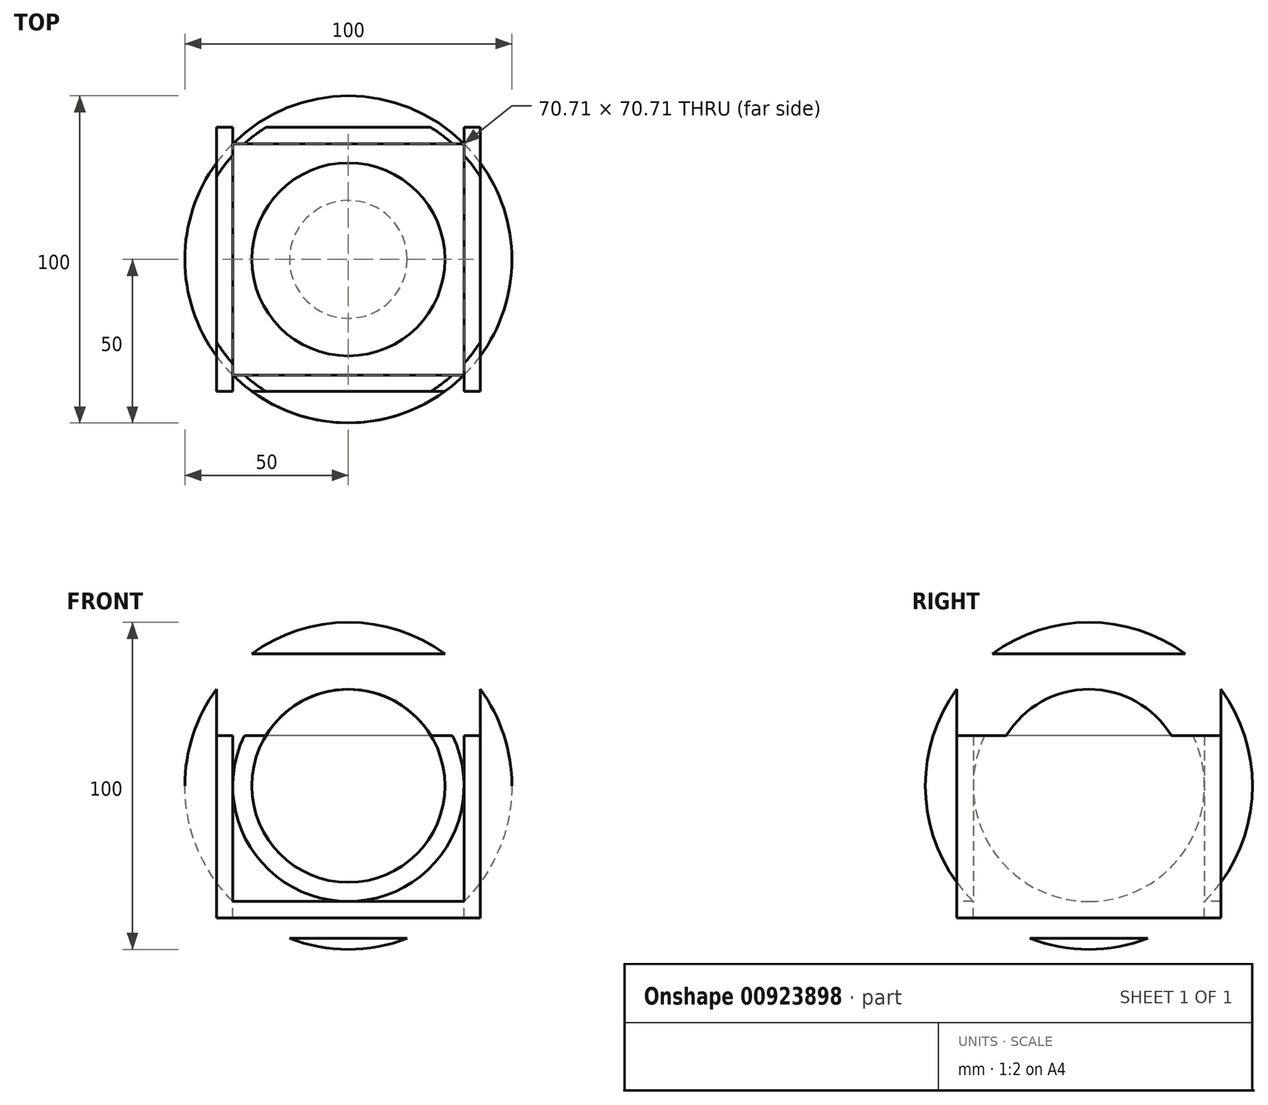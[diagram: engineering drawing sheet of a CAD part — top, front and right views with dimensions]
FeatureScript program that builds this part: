
annotation { "Feature Type Name" : "Feature", "Feature Type Description" : "" }
export const myFeature = defineFeature(function(context is Context, id is Id, definition is map)
    precondition{}
    {
        {
            var Q0;
            Q0=qCreatedBy(makeId("Front.planeOp"),FACE);
            var sketch = newSketch(context, id + "F0", { "sketchPlane" : qUnion([Q0])});
            skCircle(sketch, "E0", {"center": v(0, 0) * mm, "radius": 50 * mm});
            skLineSegment(sketch, "E1.bottom", {"start": v(40.36, -40.36) * mm, "end": v(-40.36, -40.36) * mm});
            skLineSegment(sketch, "E1.top", {"start": v(40.36, 40.36) * mm, "end": v(-40.36, 40.36) * mm});
            skLineSegment(sketch, "E1.left", {"start": v(40.36, -40.36) * mm, "end": v(40.36, 40.36) * mm});
            skLineSegment(sketch, "E1.right", {"start": v(-40.36, -40.36) * mm, "end": v(-40.36, 40.36) * mm});
            skLineSegment(sketch, "E2.0", {"start": v(35.36, 35.36) * mm, "end": v(-35.36, 35.36) * mm});
            skLineSegment(sketch, "E2.1", {"start": v(35.36, -35.36) * mm, "end": v(35.36, 35.36) * mm});
            skLineSegment(sketch, "E2.2", {"start": v(35.36, -35.36) * mm, "end": v(-35.36, -35.36) * mm});
            skLineSegment(sketch, "E2.3", {"start": v(-35.36, -35.36) * mm, "end": v(-35.36, 35.36) * mm});
            skLineSegment(sketch, "E3", {"start": v(0, 0) * mm, "end": v(0, 62.81) * mm, "construction": true});
            skLineSegment(sketch, "E4", {"start": v(0, 0) * mm, "end": v(91.75, 0) * mm, "construction": true});
            skLineSegment(sketch, "E5.bottom", {"start": v(35.36, 35.36) * mm, "end": v(40.36, 35.36) * mm});
            skLineSegment(sketch, "E5.top", {"start": v(35.36, 40.36) * mm, "end": v(40.36, 40.36) * mm});
            skLineSegment(sketch, "E5.left", {"start": v(35.36, 35.36) * mm, "end": v(35.36, 40.36) * mm});
            skLineSegment(sketch, "E5.right", {"start": v(40.36, 35.36) * mm, "end": v(40.36, 40.36) * mm});
            skLineSegment(sketch, "E6.bottom", {"start": v(-40.36, 40.36) * mm, "end": v(-35.36, 40.36) * mm});
            skLineSegment(sketch, "E6.top", {"start": v(-40.36, 35.36) * mm, "end": v(-35.36, 35.36) * mm});
            skLineSegment(sketch, "E6.left", {"start": v(-40.36, 40.36) * mm, "end": v(-40.36, 35.36) * mm});
            skLineSegment(sketch, "E6.right", {"start": v(-35.36, 40.36) * mm, "end": v(-35.36, 35.36) * mm});
            skLineSegment(sketch, "E7.bottom", {"start": v(-40.36, -40.36) * mm, "end": v(-35.36, -40.36) * mm});
            skLineSegment(sketch, "E7.top", {"start": v(-40.36, -35.36) * mm, "end": v(-35.36, -35.36) * mm});
            skLineSegment(sketch, "E7.left", {"start": v(-40.36, -40.36) * mm, "end": v(-40.36, -35.36) * mm});
            skLineSegment(sketch, "E7.right", {"start": v(-35.36, -40.36) * mm, "end": v(-35.36, -35.36) * mm});
            skLineSegment(sketch, "E8.bottom", {"start": v(35.36, -35.36) * mm, "end": v(40.36, -35.36) * mm});
            skLineSegment(sketch, "E8.top", {"start": v(35.36, -40.36) * mm, "end": v(40.36, -40.36) * mm});
            skLineSegment(sketch, "E8.left", {"start": v(35.36, -35.36) * mm, "end": v(35.36, -40.36) * mm});
            skLineSegment(sketch, "E8.right", {"start": v(40.36, -35.36) * mm, "end": v(40.36, -40.36) * mm});
            skSolve(sketch);
        }
        {
            var Q0;
            Q0=qCreatedBy(makeId("Right.planeOp"),FACE);
            var sketch = newSketch(context, id + "F1", { "sketchPlane" : qUnion([Q0])});
            skCircle(sketch, "E9", {"center": v(0, 0) * mm, "radius": 50 * mm});
            skLineSegment(sketch, "E10.bottom", {"start": v(40.36, 40.36) * mm, "end": v(-40.36, 40.36) * mm});
            skLineSegment(sketch, "E10.top", {"start": v(40.36, -40.36) * mm, "end": v(-40.36, -40.36) * mm});
            skLineSegment(sketch, "E10.left", {"start": v(40.36, 40.36) * mm, "end": v(40.36, -40.36) * mm});
            skLineSegment(sketch, "E10.right", {"start": v(-40.36, 40.36) * mm, "end": v(-40.36, -40.36) * mm});
            skLineSegment(sketch, "E11.0", {"start": v(35.36, 35.36) * mm, "end": v(-35.36, 35.36) * mm});
            skLineSegment(sketch, "E11.1", {"start": v(35.36, 35.36) * mm, "end": v(35.36, -35.36) * mm});
            skLineSegment(sketch, "E11.2", {"start": v(35.36, -35.36) * mm, "end": v(-35.36, -35.36) * mm});
            skLineSegment(sketch, "E11.3", {"start": v(-35.36, 35.36) * mm, "end": v(-35.36, -35.36) * mm});
            skLineSegment(sketch, "E12.bottom", {"start": v(-40.36, 40.36) * mm, "end": v(-35.36, 40.36) * mm});
            skLineSegment(sketch, "E12.top", {"start": v(-40.36, 35.36) * mm, "end": v(-35.36, 35.36) * mm});
            skLineSegment(sketch, "E12.left", {"start": v(-40.36, 40.36) * mm, "end": v(-40.36, 35.36) * mm});
            skLineSegment(sketch, "E12.right", {"start": v(-35.36, 40.36) * mm, "end": v(-35.36, 35.36) * mm});
            skLineSegment(sketch, "E13.bottom", {"start": v(40.36, 40.36) * mm, "end": v(35.36, 40.36) * mm});
            skLineSegment(sketch, "E13.top", {"start": v(40.36, 35.36) * mm, "end": v(35.36, 35.36) * mm});
            skLineSegment(sketch, "E13.left", {"start": v(40.36, 40.36) * mm, "end": v(40.36, 35.36) * mm});
            skLineSegment(sketch, "E13.right", {"start": v(35.36, 40.36) * mm, "end": v(35.36, 35.36) * mm});
            skLineSegment(sketch, "E14.bottom", {"start": v(40.36, -40.36) * mm, "end": v(35.36, -40.36) * mm});
            skLineSegment(sketch, "E14.top", {"start": v(40.36, -35.36) * mm, "end": v(35.36, -35.36) * mm});
            skLineSegment(sketch, "E14.left", {"start": v(40.36, -40.36) * mm, "end": v(40.36, -35.36) * mm});
            skLineSegment(sketch, "E14.right", {"start": v(35.36, -40.36) * mm, "end": v(35.36, -35.36) * mm});
            skLineSegment(sketch, "E15.bottom", {"start": v(-40.36, -40.36) * mm, "end": v(-35.36, -40.36) * mm});
            skLineSegment(sketch, "E15.top", {"start": v(-40.36, -35.36) * mm, "end": v(-35.36, -35.36) * mm});
            skLineSegment(sketch, "E15.left", {"start": v(-40.36, -40.36) * mm, "end": v(-40.36, -35.36) * mm});
            skLineSegment(sketch, "E15.right", {"start": v(-35.36, -40.36) * mm, "end": v(-35.36, -35.36) * mm});
            skSolve(sketch);
        }
        {
            var Q0;
            Q0=qCreatedBy(makeId("Front.planeOp"),FACE);
            var sketch = newSketch(context, id + "F2", { "sketchPlane" : qUnion([Q0])});
            skArc(sketch, "E16.0", {"start": v(50, 0) * mm, "mid": v(0, 50) * mm, "end": v(-50, 0) * mm});
            skLineSegment(sketch, "E17", {"start": v(-50, 0) * mm, "end": v(50, 0) * mm});
            skSolve(sketch);
        }
        {
            var Q0;
            Q0 = qSketchRegion(id + "F2", true);
            var Q1;
            Q1=sQuery(id+"F0.wireOp",EDGE,"E4");
            revolve(context, id + "F3", {"surfaceOperationType" : NewSurfaceOperationType.NEW, "entities" : qUnion([Q0]), "axis" : qUnion([Q1]), "revolveType" : RevolveType.FULL});
        }
        {
            var Q0;
            Q0=qCreatedBy(makeId("Front.planeOp"),FACE);
            var sketch = newSketch(context, id + "F4", { "sketchPlane" : qUnion([Q0])});
            skLineSegment(sketch, "E18.0", {"start": v(40.36, -40.36) * mm, "end": v(40.36, 40.36) * mm});
            skLineSegment(sketch, "E18.1", {"start": v(40.36, -40.36) * mm, "end": v(-40.36, -40.36) * mm});
            skLineSegment(sketch, "E18.2", {"start": v(-40.36, -40.36) * mm, "end": v(-40.36, 40.36) * mm});
            skLineSegment(sketch, "E18.3", {"start": v(40.36, 40.36) * mm, "end": v(-40.36, 40.36) * mm});
            skSolve(sketch);
        }
        {
            var Q0;
            Q0 = qSketchRegion(id + "F4", true);
            var Q1;
            Q1=sQuery(id+"F1.wireOp",VERTEX,"E10.top.start");
            var Q2;
            Q2=sQuery(id+"F1.wireOp",VERTEX,"E10.top.end");
            extrude(context, id + "F5", {"entities" : qUnion([Q0]), "endBound" : BoundingType.UP_TO_VERTEX, "oppositeDirection" : true, "depth" : 25 * mm, "endBoundEntityVertex" : qUnion([Q1]), "offsetDistance" : 25 * mm, "hasSecondDirection" : true, "secondDirectionBound" : SecondDirectionBoundingType.UP_TO_VERTEX, "secondDirectionOppositeDirection" : false, "secondDirectionDepth" : 25 * mm, "secondDirectionBoundEntityVertex" : qUnion([Q2])});
        }
        {
            var Q0;
            {var subQ3=sQuery(id+"F0.wireOp",EDGE,"E2.0");Q0=makeQuery(id+"F0.imprint","IMPRINT",FACE,{"disambiguationData":[TD([[makeQuery(id+"F0.imprint","IMPRINT",EDGE,{"derivedFrom":subQ3}),-1.0]])]});}
            var Q1;
            {var subQ0=sQuery(id+"F0.wireOp",EDGE,"E6.right");Q1=makeQuery(id+"F0.imprint","IMPRINT",FACE,{"disambiguationData":[TD([[makeQuery(id+"F0.imprint","IMPRINT",EDGE,{"derivedFrom":subQ0}),1.0]])]});}
            var Q2;
            {var subQ4=sQuery(id+"F0.wireOp",EDGE,"E6.top");Q2=makeQuery(id+"F0.imprint","IMPRINT",FACE,{"disambiguationData":[TD([[makeQuery(id+"F0.imprint","IMPRINT",EDGE,{"derivedFrom":subQ4}),1.0]])]});}
            var Q3;
            {var subQ0=sQuery(id+"F0.wireOp",EDGE,"E6.top");Q3=makeQuery(id+"F0.imprint","IMPRINT",FACE,{"disambiguationData":[TD([[makeQuery(id+"F0.imprint","IMPRINT",EDGE,{"derivedFrom":subQ0}),-1.0]])]});}
            var Q4;
            {var subQ0=sQuery(id+"F0.wireOp",EDGE,"E2.3");Q4=makeQuery(id+"F0.imprint","IMPRINT",FACE,{"disambiguationData":[TD([[makeQuery(id+"F0.imprint","IMPRINT",EDGE,{"derivedFrom":subQ0}),1.0]])]});}
            var Q5;
            {var subQ3=sQuery(id+"F0.wireOp",EDGE,"E7.top");Q5=makeQuery(id+"F0.imprint","IMPRINT",FACE,{"disambiguationData":[TD([[makeQuery(id+"F0.imprint","IMPRINT",EDGE,{"derivedFrom":subQ3}),1.0]])]});}
            var Q6;
            {var subQ4=sQuery(id+"F0.wireOp",EDGE,"E7.top");Q6=makeQuery(id+"F0.imprint","IMPRINT",FACE,{"disambiguationData":[TD([[makeQuery(id+"F0.imprint","IMPRINT",EDGE,{"derivedFrom":subQ4}),-1.0]])]});}
            var Q7;
            {var subQ0=sQuery(id+"F0.wireOp",EDGE,"E7.right");Q7=makeQuery(id+"F0.imprint","IMPRINT",FACE,{"disambiguationData":[TD([[makeQuery(id+"F0.imprint","IMPRINT",EDGE,{"derivedFrom":subQ0}),-1.0]])]});}
            var Q8;
            {var subQ3=sQuery(id+"F0.wireOp",EDGE,"E2.2");Q8=makeQuery(id+"F0.imprint","IMPRINT",FACE,{"disambiguationData":[TD([[makeQuery(id+"F0.imprint","IMPRINT",EDGE,{"derivedFrom":subQ3}),1.0]])]});}
            var Q9;
            {var subQ3=sQuery(id+"F0.wireOp",EDGE,"E8.left");Q9=makeQuery(id+"F0.imprint","IMPRINT",FACE,{"disambiguationData":[TD([[makeQuery(id+"F0.imprint","IMPRINT",EDGE,{"derivedFrom":subQ3}),-1.0]])]});}
            var Q10;
            {var subQ4=sQuery(id+"F0.wireOp",EDGE,"E8.bottom");Q10=makeQuery(id+"F0.imprint","IMPRINT",FACE,{"disambiguationData":[TD([[makeQuery(id+"F0.imprint","IMPRINT",EDGE,{"derivedFrom":subQ4}),-1.0]])]});}
            var Q11;
            {var subQ3=sQuery(id+"F0.wireOp",EDGE,"E8.bottom");Q11=makeQuery(id+"F0.imprint","IMPRINT",FACE,{"disambiguationData":[TD([[makeQuery(id+"F0.imprint","IMPRINT",EDGE,{"derivedFrom":subQ3}),1.0]])]});}
            var Q12;
            {var subQ3=sQuery(id+"F0.wireOp",EDGE,"E2.1");Q12=makeQuery(id+"F0.imprint","IMPRINT",FACE,{"disambiguationData":[TD([[makeQuery(id+"F0.imprint","IMPRINT",EDGE,{"derivedFrom":subQ3}),-1.0]])]});}
            var Q13;
            {var subQ3=sQuery(id+"F0.wireOp",EDGE,"E5.left");Q13=makeQuery(id+"F0.imprint","IMPRINT",FACE,{"disambiguationData":[TD([[makeQuery(id+"F0.imprint","IMPRINT",EDGE,{"derivedFrom":subQ3}),1.0]])]});}
            var Q14;
            {var subQ4=sQuery(id+"F0.wireOp",EDGE,"E5.bottom");Q14=makeQuery(id+"F0.imprint","IMPRINT",FACE,{"disambiguationData":[TD([[makeQuery(id+"F0.imprint","IMPRINT",EDGE,{"derivedFrom":subQ4}),1.0]])]});}
            var Q15;
            {var subQ0=sQuery(id+"F0.wireOp",EDGE,"E5.bottom");Q15=makeQuery(id+"F0.imprint","IMPRINT",FACE,{"disambiguationData":[TD([[makeQuery(id+"F0.imprint","IMPRINT",EDGE,{"derivedFrom":subQ0}),-1.0]])]});}
            var Q16;
            Q16=sQuery(id+"F1.wireOp",VERTEX,"E10.bottom.end");
            var Q17;
            Q17=sQuery(id+"F1.wireOp",VERTEX,"E10.top.start");
            extrude(context, id + "F6", {"entities" : qUnion([Q0, Q1, Q2, Q3, Q4, Q5, Q6, Q7, Q8, Q9, Q10, Q11, Q12, Q13, Q14, Q15]), "endBound" : BoundingType.UP_TO_VERTEX, "depth" : 25 * mm, "endBoundEntityVertex" : qUnion([Q16]), "offsetDistance" : 25 * mm, "hasSecondDirection" : true, "secondDirectionBound" : SecondDirectionBoundingType.UP_TO_VERTEX, "secondDirectionOppositeDirection" : true, "secondDirectionDepth" : 25 * mm, "secondDirectionBoundEntityVertex" : qUnion([Q17])});
        }
        {
            var Q0;
            Q0=sQuery(id+"F1.wireOp",EDGE,"E10.bottom");
            var Q1;
            Q1=sQuery(id+"F1.wireOp",EDGE,"E10.right");
            var Q2;
            Q2=sQuery(id+"F1.wireOp",EDGE,"E11.3");
            var Q3;
            Q3=sQuery(id+"F1.wireOp",EDGE,"E11.0");
            var Q4;
            Q4=sQuery(id+"F1.wireOp",EDGE,"E11.1");
            var Q5;
            Q5=sQuery(id+"F1.wireOp",EDGE,"E10.left");
            var Q6;
            Q6=sQuery(id+"F1.wireOp",EDGE,"E10.top");
            var Q7;
            Q7=sQuery(id+"F1.wireOp",EDGE,"E11.2");
            var Q8;
            Q8=makeQuery(id+"F6.opExtrude","CAP_VERTEX",VERTEX,{"disambiguationData":[OSD([sQuery(id+"F0.wireOp",EDGE,"E1.top"),sQuery(id+"F0.wireOp",EDGE,"E1.left")])],"isStart":true});
            var Q9;
            Q9=makeQuery(id+"F6.opExtrude","CAP_VERTEX",VERTEX,{"disambiguationData":[OSD([sQuery(id+"F0.wireOp",EDGE,"E1.top"),sQuery(id+"F0.wireOp",EDGE,"E1.right")])],"isStart":true});
            extrude(context, id + "F7", {"bodyType" : ToolBodyType.SURFACE, "surfaceEntities" : qUnion([Q0, Q1, Q2, Q3, Q4, Q5, Q6, Q7]), "endBound" : BoundingType.UP_TO_VERTEX, "depth" : 25 * mm, "endBoundEntityVertex" : qUnion([Q8]), "offsetDistance" : 25 * mm, "hasSecondDirection" : true, "secondDirectionBound" : SecondDirectionBoundingType.UP_TO_VERTEX, "secondDirectionOppositeDirection" : true, "secondDirectionDepth" : 25 * mm, "secondDirectionBoundEntityVertex" : qUnion([Q9])});
        }
        {
            var Q0;
            Q0=makeQuery(id+"F5.opExtrude","CAP_FACE",FACE,{"disambiguationData":[OSD([sQuery(id+"F4.wireOp",EDGE,"E18.0"),sQuery(id+"F4.wireOp",EDGE,"E18.1"),sQuery(id+"F4.wireOp",EDGE,"E18.2"),sQuery(id+"F4.wireOp",EDGE,"E18.3")])],"isStart":true});
            var sketch = newSketch(context, id + "F8", { "sketchPlane" : qUnion([Q0])});
            skLineSegment(sketch, "E19.0", {"start": v(35.36, 35.36) * mm, "end": v(-35.36, 35.36) * mm});
            skLineSegment(sketch, "E19.1", {"start": v(-35.36, -35.36) * mm, "end": v(-35.36, 35.36) * mm});
            skLineSegment(sketch, "E19.2", {"start": v(35.36, -35.36) * mm, "end": v(35.36, 35.36) * mm});
            skLineSegment(sketch, "E19.3", {"start": v(35.36, -35.36) * mm, "end": v(-35.36, -35.36) * mm});
            skSolve(sketch);
        }
        {
            var Q0;
            Q0 = qSketchRegion(id + "F8", true);
            extrude(context, id + "F9", {"entities" : qUnion([Q0]), "operationType" : NewBodyOperationType.REMOVE, "endBound" : BoundingType.THROUGH_ALL, "oppositeDirection" : true, "depth" : 25 * mm, "offsetDistance" : 25 * mm});
        }
        {
            var Q0;
            Q0 = qSketchRegion(id + "F2", true);
            var Q1;
            Q1=sQuery(id+"F0.wireOp",EDGE,"E4");
            revolve(context, id + "F10", {"surfaceOperationType" : NewSurfaceOperationType.NEW, "entities" : qUnion([Q0]), "axis" : qUnion([Q1]), "revolveType" : RevolveType.FULL});
        }
        {
            var Q0;
            Q0=makeQuery(id+"F5.opExtrude","SWEPT_FACE",FACE,{"disambiguationData":[OSD([sQuery(id+"F4.wireOp",EDGE,"E18.3")])]});
            var sketch = newSketch(context, id + "F11", { "sketchPlane" : qUnion([Q0])});
            skLineSegment(sketch, "E20.1", {"start": v(-40.36, 40.36) * mm, "end": v(-40.36, -40.36) * mm});
            skLineSegment(sketch, "E20.2", {"start": v(40.36, 40.36) * mm, "end": v(-40.36, 40.36) * mm});
            skLineSegment(sketch, "E20.3", {"start": v(40.36, 40.36) * mm, "end": v(40.36, -40.36) * mm});
            skLineSegment(sketch, "E20.4", {"start": v(40.36, -40.36) * mm, "end": v(-40.36, -40.36) * mm});
            skLineSegment(sketch, "E21.0", {"start": v(35.36, 35.36) * mm, "end": v(-35.36, 35.36) * mm});
            skLineSegment(sketch, "E21.1", {"start": v(35.36, 35.36) * mm, "end": v(35.36, -35.36) * mm});
            skLineSegment(sketch, "E21.2", {"start": v(35.36, -35.36) * mm, "end": v(-35.36, -35.36) * mm});
            skLineSegment(sketch, "E21.3", {"start": v(-35.36, 35.36) * mm, "end": v(-35.36, -35.36) * mm});
            skSolve(sketch);
        }
        {
            var Q0;
            Q0 = qSketchRegion(id + "F11", true);
            extrude(context, id + "F12", {"entities" : qUnion([Q0]), "operationType" : NewBodyOperationType.REMOVE, "oppositeDirection" : true, "depth" : 25 * mm, "offsetDistance" : 25 * mm});
        }
        {
            var Q0;
            Q0=makeQuery(id+"F5.opExtrude","SWEPT_FACE",FACE,{"disambiguationData":[OSD([sQuery(id+"F4.wireOp",EDGE,"E18.3")])]});
            extrude(context, id + "F13", {"entities" : qUnion([Q0]), "operationType" : NewBodyOperationType.REMOVE, "oppositeDirection" : true, "depth" : 87 * mm, "offsetDistance" : 25 * mm});
        }
    });
